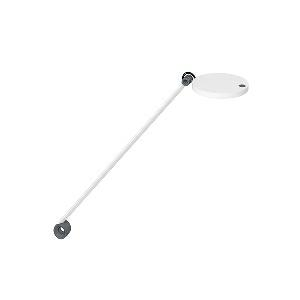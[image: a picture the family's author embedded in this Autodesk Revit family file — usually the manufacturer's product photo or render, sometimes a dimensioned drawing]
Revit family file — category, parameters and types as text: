
# Revit family: para_mi_-_mftl_102_r__930_00632665_039f
name_source: partatom
category: Lighting Fixtures
units: mm (PartAtom-declared; Revit-internal decimal feet)

## family parameters
Cut with Voids When Loaded = No
Host = Face
Light Source = No
Part Type = Normal
Room Calculation Point = No
Round Connector Dimension = Use Diameter
Shared = No

## types (1)
- PARA.MI - MFTL 102 R /930 (1 x LED, 580 lm, 3000K)
    Apparent Load = 7 VA
    Approval mark = CE
    CIE Flux Codes = 69 94 99 100 100
    Color Rendering = 90-100
    Color Temperature = 3000K
    Control Gear = Electronic ballast
    Default Elevation = 1800 mm
    Description = MFTL 102 R|Task luminaire|light source: LED|work equipment: Electronic plug-in transformer|connected load: 100-240 V, 50/60 Hz|Power consumption: approx. 7 W|luminous flux: 580 lm|luminous efficacy: 82 lm/W|Illuminance efficiency factor: 107 lx/W|colour temperature: Warm white, ca. 3000 K|color rendering index (CRI): >= 90|chromaticity tolerance:  3 SDCM|class of protection: II with plug-in power supply, III without plug-in power supply|technology: Continuously dimmable|luminaire body|material: Aluminium|surface: Painted|colour: White|lamp cover: Plastic, Clear|tubular sections|material: Tubular aluminium section|surface: Painted|colour: White|weight (net): approx. 0.8 kg|mains lead: 3.00 m Mains plug BS 1363, CEE 7/XVI, NEMA 1-15P|Fastening: Adaptor (accessory), Table base (accessory), Table clamp (accessory), Tap16|glare control: Reflector|special features: Automatic switchoff adjustable, Push button in luminaire head, Behaviour at net recovery adjustable|Approval mark: C - ETL - US (F. CAN U. USA), VDE - ENEC SEP LIGHT & POWER SUPPLY UNIT|
    Height = 12 mm  [stored 0.0393701 ft]
    Lamp = 1 x LED
    Lamp Light Flux = 580 lm
    Lamp count = 1
    Length = 123 mm
    Luminous efficacy = 83 lm/W
    Manufacturer = Waldmann
    ModVariant = No
    Model = 00632665
    Mounting Place = Table
    Mounting Type = Surface mounted
    Number of Poles = 1
    OnlyDefault = Yes
    Power Factor = 1
    Product Name = PARA.MI - MFTL 102 R /930
    Product group = Task luminaire (office)
    ProductGroupID = 21
    Protection Class = Protection class II
    Protection Degree = IP 40
    RLX_Detail_Level = 1
    RLX_Emergency_Light_Flux = 0 lm
    RLX_Emergency_Type = 0
    RLX_Emergency_Type_DB = No
    RlxData = <blob elided: 55509 chars, md5=ee79575a>
    Socket = socket
    Standby Power = 0 W
    System Light Flux = 580 lm
    System Power = 7 W
    Type Comments = Product without accessories
    Type Image = 113150000-00638520.jpg
    URL = http://relux.com
    VarID = ---
    Voltage = 230 V
    Voltage Range = 220-240 V
    Weight = 0.00 kg
    Width = 0 mm  [stored 0 ft]

note: [stored X ft] marks values corroborated as IEEE doubles in the binary element streams (Revit-internal decimal feet)

## geometry (parser evidence)
native form markers: Blend x4, Sweep x14
no freeform markers — native parametric forms only
